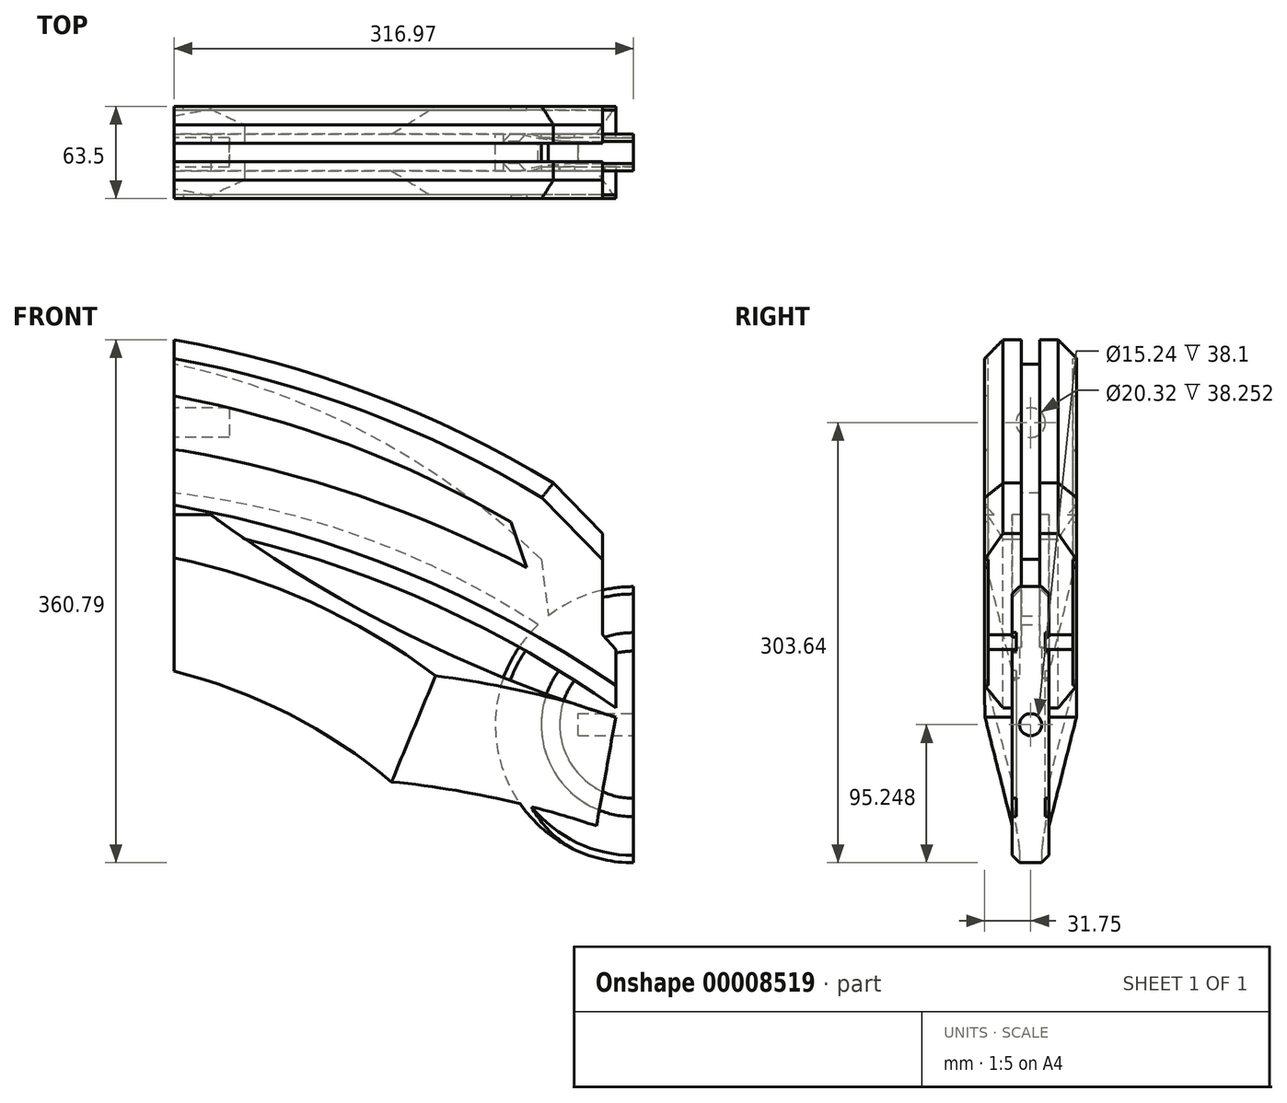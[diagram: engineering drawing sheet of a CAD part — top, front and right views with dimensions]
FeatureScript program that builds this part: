
annotation { "Feature Type Name" : "Feature", "Feature Type Description" : "" }
export const myFeature = defineFeature(function(context is Context, id is Id, definition is map)
    precondition{}
    {
        {
            var Q0;
            Q0=qCreatedBy(makeId("Right.planeOp"),FACE);
            var sketch = newSketch(context, id + "F0", { "sketchPlane" : qUnion([Q0])});
            skCircle(sketch, "E0", {"center": v(0, 0) * mm, "radius": 9.53 * mm});
            skSolve(sketch);
        }
        {
            var Q0;
            Q0=makeQuery(id+"F0.imprint","IMPRINT",FACE,{"disambiguationData":[TD([[makeQuery(id+"F0.imprint","IMPRINT",EDGE,{"derivedFrom":sQuery(id+"F0.wireOp",EDGE,"E0")}),1.0]])]});
            extrude(context, id + "F1", {"entities" : qUnion([Q0]), "depth" : 38.1 * mm});
        }
        {
            var Q0;
            Q0=qCreatedBy(makeId("Front.planeOp"),FACE);
            var sketch = newSketch(context, id + "F2", { "sketchPlane" : qUnion([Q0])});
            skLineSegment(sketch, "E1", {"start": v(37.95, -69.85) * mm, "end": v(37.95, 57.15) * mm});
            skLineSegment(sketch, "E2", {"start": v(342.75, -156.44) * mm, "end": v(342.75, -196.85) * mm});
            skArc(sketch, "E3", {"start": v(299.75, -41.71) * mm, "mid": v(173.43, 19.84) * mm, "end": v(37.95, 57.15) * mm});
            skArc(sketch, "E4", {"start": v(342.75, -196.85) * mm, "mid": v(197.3, -116.64) * mm, "end": v(37.95, -69.85) * mm});
            skLineSegment(sketch, "E5", {"start": v(342.75, -156.44) * mm, "end": v(333.76, -146.22) * mm});
            skLineSegment(sketch, "E6", {"start": v(333.76, -146.22) * mm, "end": v(333.76, -76.46) * mm});
            skLineSegment(sketch, "E7", {"start": v(333.76, -76.46) * mm, "end": v(299.75, -41.71) * mm});
            skSolve(sketch);
        }
        {
            var Q0;
            Q0=makeQuery(id+"F2.imprint","IMPRINT",FACE,{"disambiguationData":[TD([[makeQuery(id+"F2.imprint","IMPRINT",EDGE,{"derivedFrom":sQuery(id+"F2.wireOp",EDGE,"E1")}),-1.0]])]});
            var Q1;
            Q1=makeQuery(id+"F2.imprint","IMPRINT",FACE,{"disambiguationData":[TD([[makeQuery(id+"F2.imprint","IMPRINT",EDGE,{"derivedFrom":sQuery(id+"F2.wireOp",EDGE,"c96b9fbb-76f4-4b25-880c-d232280712f3")}),-1.0]])]});
            extrude(context, id + "F3", {"entities" : qUnion([Q0, Q1]), "operationType" : NewBodyOperationType.ADD, "depth" : 63.5 * mm, "symmetric" : true});
        }
        {
            var Q0;
            Q0=qCreatedBy(makeId("Front.planeOp"),FACE);
            var sketch = newSketch(context, id + "F4", { "sketchPlane" : qUnion([Q0])});
            skLineSegment(sketch, "E8.0", {"start": v(37.95, -69.85) * mm, "end": v(37.95, -48.49) * mm});
            skArc(sketch, "E8.1", {"start": v(299.75, -41.71) * mm, "mid": v(173.43, 19.84) * mm, "end": v(37.95, 57.15) * mm});
            skLineSegment(sketch, "E8.2", {"start": v(333.76, -76.46) * mm, "end": v(299.75, -41.71) * mm});
            skLineSegment(sketch, "E8.3", {"start": v(333.76, -146.22) * mm, "end": v(333.76, -76.46) * mm});
            skLineSegment(sketch, "E8.4", {"start": v(342.75, -156.44) * mm, "end": v(333.76, -146.22) * mm});
            skLineSegment(sketch, "E8.5", {"start": v(342.75, -156.44) * mm, "end": v(342.75, -196.85) * mm});
            skArc(sketch, "E8.6", {"start": v(342.75, -196.85) * mm, "mid": v(197.3, -116.64) * mm, "end": v(37.95, -69.85) * mm});
            skLineSegment(sketch, "E9.trimOffspring", {"start": v(37.95, 40.42) * mm, "end": v(37.95, 57.15) * mm});
            skArc(sketch, "E10", {"start": v(297.91, -145.2) * mm, "mid": v(173.78, -81.12) * mm, "end": v(37.95, -48.49) * mm});
            skArc(sketch, "E11", {"start": v(291.38, -94.3) * mm, "mid": v(174.1, -9.17) * mm, "end": v(37.95, 40.42) * mm});
            skLineSegment(sketch, "E12", {"start": v(291.38, -94.3) * mm, "end": v(297.91, -145.2) * mm});
            skSolve(sketch);
        }
        {
            var Q0;
            Q0 = qSketchRegion(id + "F4", true);
            extrude(context, id + "F5", {"entities" : qUnion([Q0]), "operationType" : NewBodyOperationType.REMOVE, "oppositeDirection" : true, "depth" : 12.7 * mm, "symmetric" : true});
        }
        {
            var Q0;
            Q0=makeQuery(id+"F3.opExtrude","CAP_EDGE",EDGE,{"disambiguationData":[OSD([sQuery(id+"F2.wireOp",EDGE,"E3")])],"isStart":false});
            var Q1;
            Q1=makeQuery(id+"F3.opExtrude","CAP_EDGE",EDGE,{"disambiguationData":[OSD([sQuery(id+"F2.wireOp",EDGE,"E7")])],"isStart":false});
            var Q2;
            Q2=makeQuery(id+"F3.opExtrude","CAP_EDGE",EDGE,{"disambiguationData":[OSD([sQuery(id+"F2.wireOp",EDGE,"E7")])],"isStart":true});
            var Q3;
            Q3=makeQuery(id+"F3.opExtrude","CAP_EDGE",EDGE,{"disambiguationData":[OSD([sQuery(id+"F2.wireOp",EDGE,"E3")])],"isStart":true});
            chamfer(context, id + "F6", {"entities" : qUnion([Q0, Q1, Q2, Q3]), "width" : 12.7 * mm, "tangentPropagation" : true});
        }
        {
            var Q0;
            Q0=makeQuery(id+"F3.opExtrude","CAP_EDGE",EDGE,{"disambiguationData":[OSD([sQuery(id+"F2.wireOp",EDGE,"E4")])],"isStart":false});
            var Q1;
            Q1=makeQuery(id+"F3.opExtrude","CAP_EDGE",EDGE,{"disambiguationData":[OSD([sQuery(id+"F2.wireOp",EDGE,"E4")])],"isStart":true});
            chamfer(context, id + "F7", {"entities" : qUnion([Q0, Q1]), "width" : 12.7 * mm, "tangentPropagation" : true});
        }
        {
            var Q0;
            Q0=qCreatedBy(makeId("Front.planeOp"),FACE);
            var sketch = newSketch(context, id + "F8", { "sketchPlane" : qUnion([Q0])});
            skLineSegment(sketch, "E13.0", {"start": v(37.95, -56.95) * mm, "end": v(37.95, 44.25) * mm});
            skFitSpline(sketch, "E13.1", {"points": [v(37.95, -69.85) * mm, v(37.95, -65.55) * mm, v(37.95, -61.25) * mm, v(37.95, -56.95) * mm]});
            skLineSegment(sketch, "E14", {"start": v(37.95, -69.85) * mm, "end": v(37.95, -171.45) * mm});
            skArc(sketch, "E15.0", {"start": v(342.75, -196.85) * mm, "mid": v(197.3, -116.64) * mm, "end": v(37.95, -69.85) * mm});
            skLineSegment(sketch, "E16", {"start": v(37.95, -63.56) * mm, "end": v(63.35, -63.56) * mm});
            skArc(sketch, "E17", {"start": v(63.35, -63.56) * mm, "mid": v(197.17, -145.14) * mm, "end": v(342.75, -203.2) * mm});
            skLineSegment(sketch, "E18", {"start": v(342.75, -203.2) * mm, "end": v(329.52, -278.24) * mm});
            skArc(sketch, "E19", {"start": v(188.13, -247.8) * mm, "mid": v(117.37, -201.1) * mm, "end": v(37.95, -171.45) * mm});
            skArc(sketch, "E20", {"start": v(329.52, -278.24) * mm, "mid": v(259.68, -259.03) * mm, "end": v(188.13, -247.8) * mm});
            skSolve(sketch);
        }
        {
            var Q0;
            Q0 = qSketchRegion(id + "F8", true);
            extrude(context, id + "F9", {"entities" : qUnion([Q0]), "operationType" : NewBodyOperationType.ADD, "depth" : 63.5 * mm, "symmetric" : true});
        }
        {
            var Q0;
            Q0=qCreatedBy(makeId("Front.planeOp"),FACE);
            var sketch = newSketch(context, id + "F10", { "sketchPlane" : qUnion([Q0])});
            skLineSegment(sketch, "E21.0", {"start": v(37.95, -69.85) * mm, "end": v(37.95, -171.45) * mm});
            skArc(sketch, "E21.1", {"start": v(188.13, -247.8) * mm, "mid": v(117.37, -201.1) * mm, "end": v(37.95, -171.45) * mm});
            skArc(sketch, "E21.2", {"start": v(329.52, -278.24) * mm, "mid": v(259.68, -259.03) * mm, "end": v(188.13, -247.8) * mm});
            skLineSegment(sketch, "E21.3", {"start": v(342.75, -203.2) * mm, "end": v(329.52, -278.24) * mm});
            skArc(sketch, "E21.4", {"start": v(63.35, -63.56) * mm, "mid": v(197.17, -145.14) * mm, "end": v(342.75, -203.2) * mm});
            skLineSegment(sketch, "E21.5", {"start": v(37.95, -63.56) * mm, "end": v(63.35, -63.56) * mm});
            skFitSpline(sketch, "E21.6", {"points": [v(37.95, -69.85) * mm, v(37.95, -65.55) * mm, v(37.95, -61.25) * mm, v(37.95, -56.95) * mm]});
            skSolve(sketch);
        }
        {
            var Q0;
            Q0 = qSketchRegion(id + "F10", true);
            extrude(context, id + "F11", {"entities" : qUnion([Q0]), "operationType" : NewBodyOperationType.REMOVE, "oppositeDirection" : true, "depth" : 25.4 * mm, "symmetric" : true});
        }
        {
            var Q0;
            Q0=makeQuery(id+"F9.opExtrude","CAP_EDGE",EDGE,{"disambiguationData":[OSD([sQuery(id+"F8.wireOp",EDGE,"E19")])],"isStart":false});
            var Q1;
            Q1=makeQuery(id+"F9.opExtrude","CAP_EDGE",EDGE,{"disambiguationData":[OSD([sQuery(id+"F8.wireOp",EDGE,"E20")])],"isStart":false});
            chamfer(context, id + "F12", {"entities" : qUnion([Q0, Q1]), "chamferType" : ChamferType.TWO_OFFSETS, "width1" : 19.05 * mm, "oppositeDirection" : false, "width2" : 76.2 * mm, "tangentPropagation" : true});
        }
        {
            var Q0;
            Q0=makeQuery(id+"F9.opExtrude","CAP_EDGE",EDGE,{"disambiguationData":[OSD([sQuery(id+"F8.wireOp",EDGE,"E20")])],"isStart":true});
            var Q1;
            Q1=makeQuery(id+"F9.opExtrude","CAP_EDGE",EDGE,{"disambiguationData":[OSD([sQuery(id+"F8.wireOp",EDGE,"E19")])],"isStart":true});
            chamfer(context, id + "F13", {"entities" : qUnion([Q0, Q1]), "chamferType" : ChamferType.TWO_OFFSETS, "width1" : 76.2 * mm, "oppositeDirection" : false, "width2" : 19.05 * mm, "tangentPropagation" : true});
        }
        {
            var Q0;
            Q0=qCreatedBy(makeId("Front.planeOp"),FACE);
            var sketch = newSketch(context, id + "F14", { "sketchPlane" : qUnion([Q0])});
            skArc(sketch, "E22", {"start": v(354.92, -113.14) * mm, "mid": v(259.67, -208.4) * mm, "end": v(354.92, -303.64) * mm});
            skFitSpline(sketch, "E23.0", {"points": [v(342.75, -203.2) * mm, v(338.34, -228.21) * mm, v(333.93, -253.23) * mm, v(329.52, -278.24) * mm]});
            skLineSegment(sketch, "E24", {"start": v(354.92, -208.4) * mm, "end": v(354.92, -303.64) * mm});
            skLineSegment(sketch, "E25", {"start": v(354.92, -303.64) * mm, "end": v(354.92, -113.14) * mm});
            skSolve(sketch);
        }
        {
            var Q0;
            Q0=makeQuery(id+"F14.imprint","IMPRINT",FACE,{"disambiguationData":[TD([[makeQuery(id+"F14.imprint","IMPRINT",EDGE,{"derivedFrom":sQuery(id+"F14.wireOp",EDGE,"E22")}),1.0]])]});
            extrude(context, id + "F15", {"entities" : qUnion([Q0]), "operationType" : NewBodyOperationType.ADD, "depth" : 25.4 * mm, "symmetric" : true});
        }
        {
            var Q0;
            {var subQ0=sQuery(id+"F14.wireOp",EDGE,"E22");var subQ1=sQuery(id+"F14.wireOp",EDGE,"E25");Q0=makeQuery(id+"F15.boolean.opBoolean","SPLIT",EDGE,{"disambiguationData":[TD([makeQuery(id+"F11.boolean.opBoolean","COPY",FACE,{"derivedFrom":makeQuery(id+"F11.opExtrude","CAP_FACE",FACE,{"disambiguationData":[OSD([sQuery(id+"F10.wireOp",EDGE,"E21.0"),sQuery(id+"F10.wireOp",EDGE,"E21.1"),sQuery(id+"F10.wireOp",EDGE,"E21.2"),sQuery(id+"F10.wireOp",EDGE,"E21.3"),sQuery(id+"F10.wireOp",EDGE,"E21.4"),sQuery(id+"F10.wireOp",EDGE,"E21.5"),sQuery(id+"F10.wireOp",EDGE,"E21.6")])],"isStart":true})}),makeQuery(id+"F12.opChamfer","BLEND_FACE",FACE,{"disambiguationData":[OSD([sQuery(id+"F8.wireOp",EDGE,"E20")])]}),makeQuery(id+"F15.opExtrude","SWEPT_FACE",FACE,{"disambiguationData":[OSD([subQ0])]}),makeQuery(id+"F15.opExtrude","CAP_FACE",FACE,{"disambiguationData":[OSD([subQ0,subQ1])],"isStart":false}),makeQuery(id+"F15.opExtrude","SWEPT_FACE",FACE,{"disambiguationData":[OSD([subQ1])]})])],"derivedFrom":makeQuery(id+"F15.opExtrude","CAP_EDGE",EDGE,{"disambiguationData":[OSD([subQ0])],"isStart":false})});}
            var Q1;
            {var subQ0=sQuery(id+"F14.wireOp",EDGE,"E22");Q1=makeQuery(id+"F15.boolean.opBoolean","SPLIT",EDGE,{"disambiguationData":[TD([makeQuery(id+"F3.opExtrude","SWEPT_FACE",FACE,{"disambiguationData":[OSD([sQuery(id+"F2.wireOp",EDGE,"E4")])]}),makeQuery(id+"F9.opExtrude","SWEPT_FACE",FACE,{"disambiguationData":[OSD([sQuery(id+"F8.wireOp",EDGE,"E17")])]}),makeQuery(id+"F11.boolean.opBoolean","COPY",FACE,{"derivedFrom":makeQuery(id+"F11.opExtrude","CAP_FACE",FACE,{"disambiguationData":[OSD([sQuery(id+"F10.wireOp",EDGE,"E21.0"),sQuery(id+"F10.wireOp",EDGE,"E21.1"),sQuery(id+"F10.wireOp",EDGE,"E21.2"),sQuery(id+"F10.wireOp",EDGE,"E21.3"),sQuery(id+"F10.wireOp",EDGE,"E21.4"),sQuery(id+"F10.wireOp",EDGE,"E21.5"),sQuery(id+"F10.wireOp",EDGE,"E21.6")])],"isStart":true})}),makeQuery(id+"F15.opExtrude","SWEPT_FACE",FACE,{"disambiguationData":[OSD([subQ0])]}),makeQuery(id+"F15.opExtrude","CAP_FACE",FACE,{"disambiguationData":[OSD([subQ0,sQuery(id+"F14.wireOp",EDGE,"E25")])],"isStart":false})])],"derivedFrom":makeQuery(id+"F15.opExtrude","CAP_EDGE",EDGE,{"disambiguationData":[OSD([subQ0])],"isStart":false})});}
            var Q2;
            {var subQ0=sQuery(id+"F14.wireOp",EDGE,"E22");var subQ1=sQuery(id+"F14.wireOp",EDGE,"E25");Q2=makeQuery(id+"F15.boolean.opBoolean","SPLIT",EDGE,{"disambiguationData":[TD([makeQuery(id+"F3.opExtrude","SWEPT_FACE",FACE,{"disambiguationData":[OSD([sQuery(id+"F2.wireOp",EDGE,"E6")])]}),makeQuery(id+"F15.opExtrude","SWEPT_FACE",FACE,{"disambiguationData":[OSD([subQ0])]}),makeQuery(id+"F15.opExtrude","CAP_FACE",FACE,{"disambiguationData":[OSD([subQ0,subQ1])],"isStart":false}),makeQuery(id+"F15.opExtrude","SWEPT_FACE",FACE,{"disambiguationData":[OSD([subQ1])]})])],"derivedFrom":makeQuery(id+"F15.opExtrude","CAP_EDGE",EDGE,{"disambiguationData":[OSD([subQ0])],"isStart":false})});}
            var Q3;
            {var subQ0=sQuery(id+"F14.wireOp",EDGE,"E22");var subQ1=sQuery(id+"F14.wireOp",EDGE,"E25");Q3=makeQuery(id+"F15.boolean.opBoolean","SPLIT",EDGE,{"disambiguationData":[TD([makeQuery(id+"F3.opExtrude","SWEPT_FACE",FACE,{"disambiguationData":[OSD([sQuery(id+"F2.wireOp",EDGE,"E6")])]}),makeQuery(id+"F15.opExtrude","SWEPT_FACE",FACE,{"disambiguationData":[OSD([subQ0])]}),makeQuery(id+"F15.opExtrude","CAP_FACE",FACE,{"disambiguationData":[OSD([subQ0,subQ1])],"isStart":true}),makeQuery(id+"F15.opExtrude","SWEPT_FACE",FACE,{"disambiguationData":[OSD([subQ1])]})])],"derivedFrom":makeQuery(id+"F15.opExtrude","CAP_EDGE",EDGE,{"disambiguationData":[OSD([subQ0])],"isStart":true})});}
            var Q4;
            {var subQ0=sQuery(id+"F14.wireOp",EDGE,"E22");Q4=makeQuery(id+"F15.boolean.opBoolean","SPLIT",EDGE,{"disambiguationData":[TD([makeQuery(id+"F3.opExtrude","SWEPT_FACE",FACE,{"disambiguationData":[OSD([sQuery(id+"F2.wireOp",EDGE,"E4")])]}),makeQuery(id+"F9.opExtrude","SWEPT_FACE",FACE,{"disambiguationData":[OSD([sQuery(id+"F8.wireOp",EDGE,"E17")])]}),makeQuery(id+"F11.boolean.opBoolean","COPY",FACE,{"derivedFrom":makeQuery(id+"F11.opExtrude","CAP_FACE",FACE,{"disambiguationData":[OSD([sQuery(id+"F10.wireOp",EDGE,"E21.0"),sQuery(id+"F10.wireOp",EDGE,"E21.1"),sQuery(id+"F10.wireOp",EDGE,"E21.2"),sQuery(id+"F10.wireOp",EDGE,"E21.3"),sQuery(id+"F10.wireOp",EDGE,"E21.4"),sQuery(id+"F10.wireOp",EDGE,"E21.5"),sQuery(id+"F10.wireOp",EDGE,"E21.6")])],"isStart":false})}),makeQuery(id+"F15.opExtrude","SWEPT_FACE",FACE,{"disambiguationData":[OSD([subQ0])]}),makeQuery(id+"F15.opExtrude","CAP_FACE",FACE,{"disambiguationData":[OSD([subQ0,sQuery(id+"F14.wireOp",EDGE,"E25")])],"isStart":true})])],"derivedFrom":makeQuery(id+"F15.opExtrude","CAP_EDGE",EDGE,{"disambiguationData":[OSD([subQ0])],"isStart":true})});}
            var Q5;
            {var subQ0=sQuery(id+"F14.wireOp",EDGE,"E22");var subQ1=sQuery(id+"F14.wireOp",EDGE,"E25");Q5=makeQuery(id+"F15.boolean.opBoolean","SPLIT",EDGE,{"disambiguationData":[TD([makeQuery(id+"F11.boolean.opBoolean","COPY",FACE,{"derivedFrom":makeQuery(id+"F11.opExtrude","CAP_FACE",FACE,{"disambiguationData":[OSD([sQuery(id+"F10.wireOp",EDGE,"E21.0"),sQuery(id+"F10.wireOp",EDGE,"E21.1"),sQuery(id+"F10.wireOp",EDGE,"E21.2"),sQuery(id+"F10.wireOp",EDGE,"E21.3"),sQuery(id+"F10.wireOp",EDGE,"E21.4"),sQuery(id+"F10.wireOp",EDGE,"E21.5"),sQuery(id+"F10.wireOp",EDGE,"E21.6")])],"isStart":false})}),makeQuery(id+"F13.opChamfer","BLEND_FACE",FACE,{"disambiguationData":[OSD([sQuery(id+"F8.wireOp",EDGE,"E20")])]}),makeQuery(id+"F15.opExtrude","SWEPT_FACE",FACE,{"disambiguationData":[OSD([subQ0])]}),makeQuery(id+"F15.opExtrude","CAP_FACE",FACE,{"disambiguationData":[OSD([subQ0,subQ1])],"isStart":true}),makeQuery(id+"F15.opExtrude","SWEPT_FACE",FACE,{"disambiguationData":[OSD([subQ1])]})])],"derivedFrom":makeQuery(id+"F15.opExtrude","CAP_EDGE",EDGE,{"disambiguationData":[OSD([subQ0])],"isStart":true})});}
            chamfer(context, id + "F16", {"entities" : qUnion([Q0, Q1, Q2, Q3, Q4, Q5]), "width" : 5.08 * mm, "tangentPropagation" : true});
        }
        {
            var Q0;
            Q0=makeQuery(id+"F3.opExtrude","CAP_FACE",FACE,{"disambiguationData":[OSD([sQuery(id+"F2.wireOp",EDGE,"E1"),sQuery(id+"F2.wireOp",EDGE,"E2"),sQuery(id+"F2.wireOp",EDGE,"E3"),sQuery(id+"F2.wireOp",EDGE,"E4"),sQuery(id+"F2.wireOp",EDGE,"E5"),sQuery(id+"F2.wireOp",EDGE,"E6"),sQuery(id+"F2.wireOp",EDGE,"E7")])],"isStart":false});
            var sketch = newSketch(context, id + "F17", { "sketchPlane" : qUnion([Q0])});
            skArc(sketch, "E26.0", {"start": v(37.95, -56.95) * mm, "mid": v(197.03, -102.8) * mm, "end": v(342.75, -181.38) * mm});
            skArc(sketch, "E26.1", {"start": v(291.8, -51.75) * mm, "mid": v(169.26, 7.84) * mm, "end": v(37.95, 44.25) * mm});
            skLineSegment(sketch, "E26.2", {"start": v(37.95, -56.95) * mm, "end": v(37.95, 44.25) * mm});
            skArc(sketch, "E27.0", {"start": v(44.52, -19.43) * mm, "mid": v(166.02, -50.54) * mm, "end": v(281.28, -99.97) * mm});
            skArc(sketch, "E28.0", {"start": v(270.5, -68.62) * mm, "mid": v(157.98, -15.06) * mm, "end": v(37.95, 18.42) * mm});
            skLineSegment(sketch, "E29", {"start": v(44.52, -19.43) * mm, "end": v(37.95, -18.78) * mm});
            skLineSegment(sketch, "E30", {"start": v(270.5, -68.62) * mm, "end": v(281.28, -99.97) * mm});
            skSolve(sketch);
        }
        {
            var Q0;
            Q0=makeQuery(id+"F17.imprint","IMPRINT",FACE,{"disambiguationData":[TD([[makeQuery(id+"F17.imprint","IMPRINT",EDGE,{"derivedFrom":sQuery(id+"F17.wireOp",EDGE,"E27.0")}),1.0]])]});
            extrude(context, id + "F18", {"entities" : qUnion([Q0]), "operationType" : NewBodyOperationType.REMOVE, "oppositeDirection" : true, "depth" : 2.54 * mm});
        }
        {
            var Q0;
            Q0=makeQuery(id+"F3.opExtrude","CAP_FACE",FACE,{"disambiguationData":[OSD([sQuery(id+"F2.wireOp",EDGE,"E1"),sQuery(id+"F2.wireOp",EDGE,"E2"),sQuery(id+"F2.wireOp",EDGE,"E3"),sQuery(id+"F2.wireOp",EDGE,"E4"),sQuery(id+"F2.wireOp",EDGE,"E5"),sQuery(id+"F2.wireOp",EDGE,"E6"),sQuery(id+"F2.wireOp",EDGE,"E7")])],"isStart":true});
            var sketch = newSketch(context, id + "F19", { "sketchPlane" : qUnion([Q0])});
            skArc(sketch, "E31.0", {"start": v(-270.5, -68.62) * mm, "mid": v(-157.98, -15.06) * mm, "end": v(-37.95, 18.42) * mm});
            skArc(sketch, "E31.1", {"start": v(-44.52, -19.43) * mm, "mid": v(-166.02, -50.54) * mm, "end": v(-281.28, -99.97) * mm});
            skLineSegment(sketch, "E31.2", {"start": v(-44.52, -19.43) * mm, "end": v(-37.95, -18.78) * mm});
            skLineSegment(sketch, "E31.3", {"start": v(-270.5, -68.62) * mm, "end": v(-281.28, -99.97) * mm});
            skSolve(sketch);
        }
        {
            var Q0;
            {var subQ2=sQuery(id+"F19.wireOp",EDGE,"E31.0");Q0=makeQuery(id+"F19.imprint","IMPRINT",FACE,{"disambiguationData":[TD([[makeQuery(id+"F19.imprint","IMPRINT",EDGE,{"derivedFrom":subQ2}),-1.0]])]});}
            extrude(context, id + "F20", {"entities" : qUnion([Q0]), "operationType" : NewBodyOperationType.REMOVE, "oppositeDirection" : true, "depth" : 2.54 * mm});
        }
        {
            var Q0;
            Q0=makeQuery(id+"F15.opExtrude","SWEPT_FACE",FACE,{"disambiguationData":[OSD([sQuery(id+"F14.wireOp",EDGE,"E25")])]});
            var sketch = newSketch(context, id + "F21", { "sketchPlane" : qUnion([Q0])});
            skLineSegment(sketch, "E32", {"start": v(0, -303.64) * mm, "end": v(0, -113.14) * mm, "construction": true});
            skCircle(sketch, "E33", {"center": v(0, -208.4) * mm, "radius": 7.62 * mm});
            skSolve(sketch);
        }
        {
            var Q0;
            Q0=makeQuery(id+"F21.imprint","IMPRINT",FACE,{"disambiguationData":[TD([[makeQuery(id+"F21.imprint","IMPRINT",EDGE,{"derivedFrom":sQuery(id+"F21.wireOp",EDGE,"E33")}),1.0]])]});
            extrude(context, id + "F22", {"entities" : qUnion([Q0]), "operationType" : NewBodyOperationType.REMOVE, "oppositeDirection" : true, "depth" : 38.1 * mm});
        }
        {
            var Q0;
            Q0=makeQuery(id+"F15.opExtrude","CAP_FACE",FACE,{"disambiguationData":[OSD([sQuery(id+"F14.wireOp",EDGE,"E22"),sQuery(id+"F14.wireOp",EDGE,"E25")])],"isStart":false});
            var sketch = newSketch(context, id + "F23", { "sketchPlane" : qUnion([Q0])});
            skLineSegment(sketch, "E34.0", {"start": v(354.92, -298.56) * mm, "end": v(354.92, -118.22) * mm});
            skCircle(sketch, "E35", {"center": v(354.92, -208.4) * mm, "radius": 50.8 * mm});
            skCircle(sketch, "E36", {"center": v(354.92, -208.4) * mm, "radius": 63.5 * mm});
            skSolve(sketch);
        }
        {
            var Q0;
            {var subQ14=sQuery(id+"F23.wireOp",EDGE,"E36");var subQ16=sQuery(id+"F23.wireOp",EDGE,"E34.0");var subQ17=makeQuery(id+"F23.imprint","INTERSECT",VERTEX,{"disambiguationData":[OD(1.0)],"derivedFrom":[subQ16,subQ14]});Q0=makeQuery(id+"F23.imprint","IMPRINT",FACE,{"disambiguationData":[TD([[makeQuery(id+"F23.imprint","IMPRINT",EDGE,{"disambiguationData":[TD([[subQ17,1.0]])],"derivedFrom":subQ16}),1.0]])]});}
            var Q1;
            {var subQ6=sQuery(id+"F23.wireOp",EDGE,"E35");var subQ10=sQuery(id+"F10.wireOp",EDGE,"E21.4");var subQ11=makeQuery(id+"F15.boolean.opBoolean","SPLIT",EDGE,{"disambiguationData":[TD([makeQuery(id+"F9.opExtrude","SWEPT_FACE",FACE,{"disambiguationData":[OSD([sQuery(id+"F8.wireOp",EDGE,"E18")])]})])],"derivedFrom":makeQuery(id+"F11.boolean.opBoolean","COPY",EDGE,{"disambiguationData":[OD(0.0)],"derivedFrom":makeQuery(id+"F11.opExtrude","CAP_EDGE",EDGE,{"disambiguationData":[OSD([subQ10])],"isStart":true})})});var subQ12=makeQuery(id+"F23.imprint","INTERSECT",VERTEX,{"derivedFrom":[subQ11,subQ6]});Q1=makeQuery(id+"F23.imprint","IMPRINT",FACE,{"disambiguationData":[TD([[makeQuery(id+"F23.imprint","IMPRINT",EDGE,{"disambiguationData":[TD([[subQ12,1.0]])],"derivedFrom":subQ6}),-1.0]])]});}
            var Q2;
            {var subQ3=sQuery(id+"F23.wireOp",EDGE,"E36");var subQ5=sQuery(id+"F23.wireOp",EDGE,"E34.0");var subQ6=makeQuery(id+"F23.imprint","INTERSECT",VERTEX,{"disambiguationData":[OD(0.0)],"derivedFrom":[subQ5,subQ3]});Q2=makeQuery(id+"F23.imprint","IMPRINT",FACE,{"disambiguationData":[TD([[makeQuery(id+"F23.imprint","IMPRINT",EDGE,{"disambiguationData":[TD([[subQ6,-1.0]])],"derivedFrom":subQ5}),1.0]])]});}
            extrude(context, id + "F24", {"entities" : qUnion([Q0, Q1, Q2]), "operationType" : NewBodyOperationType.REMOVE, "oppositeDirection" : true, "depth" : 2.8 * mm});
        }
        {
            var Q0;
            Q0=makeQuery(id+"F15.opExtrude","CAP_FACE",FACE,{"disambiguationData":[OSD([sQuery(id+"F14.wireOp",EDGE,"E22"),sQuery(id+"F14.wireOp",EDGE,"E25")])],"isStart":true});
            var sketch = newSketch(context, id + "F25", { "sketchPlane" : qUnion([Q0])});
            skLineSegment(sketch, "E37.0", {"start": v(-354.92, -298.56) * mm, "end": v(-354.92, -118.22) * mm});
            skCircle(sketch, "E38", {"center": v(-354.92, -208.4) * mm, "radius": 50.8 * mm});
            skCircle(sketch, "E39", {"center": v(-354.92, -208.4) * mm, "radius": 63.5 * mm});
            skSolve(sketch);
        }
        {
            var Q0;
            {var subQ14=sQuery(id+"F25.wireOp",EDGE,"E39");var subQ16=sQuery(id+"F25.wireOp",EDGE,"E37.0");var subQ17=makeQuery(id+"F25.imprint","INTERSECT",VERTEX,{"disambiguationData":[OD(1.0)],"derivedFrom":[subQ16,subQ14]});Q0=makeQuery(id+"F25.imprint","IMPRINT",FACE,{"disambiguationData":[TD([[makeQuery(id+"F25.imprint","IMPRINT",EDGE,{"disambiguationData":[TD([[subQ17,1.0]])],"derivedFrom":subQ16}),-1.0]])]});}
            var Q1;
            {var subQ6=sQuery(id+"F25.wireOp",EDGE,"E38");var subQ10=sQuery(id+"F10.wireOp",EDGE,"E21.4");var subQ11=makeQuery(id+"F15.boolean.opBoolean","SPLIT",EDGE,{"disambiguationData":[TD([makeQuery(id+"F9.opExtrude","SWEPT_FACE",FACE,{"disambiguationData":[OSD([sQuery(id+"F8.wireOp",EDGE,"E18")])]})])],"derivedFrom":makeQuery(id+"F11.boolean.opBoolean","COPY",EDGE,{"disambiguationData":[OD(0.0)],"derivedFrom":makeQuery(id+"F11.opExtrude","CAP_EDGE",EDGE,{"disambiguationData":[OSD([subQ10])],"isStart":false})})});var subQ12=makeQuery(id+"F25.imprint","INTERSECT",VERTEX,{"derivedFrom":[subQ11,subQ6]});Q1=makeQuery(id+"F25.imprint","IMPRINT",FACE,{"disambiguationData":[TD([[makeQuery(id+"F25.imprint","IMPRINT",EDGE,{"disambiguationData":[TD([[subQ12,-1.0]])],"derivedFrom":subQ6}),-1.0]])]});}
            var Q2;
            {var subQ3=sQuery(id+"F25.wireOp",EDGE,"E39");var subQ5=sQuery(id+"F25.wireOp",EDGE,"E37.0");var subQ7=makeQuery(id+"F25.imprint","INTERSECT",VERTEX,{"disambiguationData":[OD(0.0)],"derivedFrom":[subQ5,subQ3]});Q2=makeQuery(id+"F25.imprint","IMPRINT",FACE,{"disambiguationData":[TD([[makeQuery(id+"F25.imprint","IMPRINT",EDGE,{"disambiguationData":[TD([[subQ7,-1.0]])],"derivedFrom":subQ5}),-1.0]])]});}
            extrude(context, id + "F26", {"entities" : qUnion([Q0, Q1, Q2]), "operationType" : NewBodyOperationType.REMOVE, "oppositeDirection" : true, "depth" : 2.54 * mm});
        }
        {
            var Q0;
            Q0=makeQuery(id+"F1.opExtrude","CAP_FACE",FACE,{"disambiguationData":[OSD([sQuery(id+"F0.wireOp",EDGE,"E0")])],"isStart":true});
            var sketch = newSketch(context, id + "F27", { "sketchPlane" : qUnion([Q0])});
            skCircle(sketch, "E40.0", {"center": v(0, 0) * mm, "radius": 9.53 * mm});
            skCircle(sketch, "E41", {"center": v(0, 0) * mm, "radius": 10.16 * mm});
            skSolve(sketch);
        }
        {
            var Q0;
            Q0 = qSketchRegion(id + "F27", true);
            var Q1;
            Q1=makeQuery(id+"F27.imprint","IMPRINT",FACE,{"disambiguationData":[TD([[makeQuery(id+"F27.imprint","IMPRINT",EDGE,{"derivedFrom":sQuery(id+"F27.wireOp",EDGE,"E40.0")}),-1.0]])]});
            extrude(context, id + "F28", {"entities" : qUnion([Q0, Q1]), "operationType" : NewBodyOperationType.REMOVE, "oppositeDirection" : true, "depth" : 76.2 * mm});
        }
    });
